# Revit family: RLV-S_Straight_DN15_External_RFA
name_source: partatom
category: Pipe Accessories
units: mm (PartAtom-declared; Revit-internal decimal feet)

## family parameters
Always vertical = Yes
Cut with Voids When Loaded = No
OmniClass Number = 23.65.55.14.17
OmniClass Title = Adjusting/Controlling Valves for Liquid Services
Part Type = Valve - Breaks Into
Round Connector Dimension = Use Diameter
Shared = No
Work Plane-Based = No

## types (2) — shared parameters
CenSd_S11_6 = 13.1 mm
CenSd_S22_6 = 15 mm  [stored 0.0492126 ft]
Connection = External thread
D = 15 mm  [stored 0.0492126 ft]
D2 = 19 mm  [stored 0.062336 ft]
D4 = 22 mm  [stored 0.0721785 ft]
D5 = 21.5 mm  [stored 0.0705381 ft]
D6 = 26.5 mm  [stored 0.0869423 ft]
DR = 20 mm  [stored 0.0656168 ft]
Description = Lockshield Valve
H2 = 21.5 mm  [stored 0.0705381 ft]
HT = 28 mm  [stored 0.0918635 ft]
IfcExportAs = IfcValveType
IfcExportType = RLV-S
Kvs = 2.2 m³/h
L2 = 22 mm  [stored 0.0721785 ft]
L3 = 7 mm  [stored 0.0229659 ft]
LOD 200 = No
LOD 350 = Yes
Manufacturer = Danfoss
Max Medium Temperature = 120 ˚C
Max Operating Pressure = 10 bar
R2 = 9.25 mm  [stored 0.0303478 ft]
RD2 = 9.5 mm  [stored 0.031168 ft]
RD5 = 10.75 mm  [stored 0.035269 ft]
RT1 = 11.2 mm  [stored 0.0367454 ft]
RV1 = 10.47 mm  [stored 0.0343504 ft]
R_thread1 = 13.22 mm  [stored 0.0433727 ft]
S11 = 15.13 mm  [stored 0.0496391 ft]
S22 = 17.32 mm
T2 = 3.5 mm  [stored 0.0114829 ft]
URL = https://store.danfoss.com
Valve Body Material = Danfoss Nickel Plated Brass
W2D = 10 mm  [stored 0.0328084 ft]
X = 11.5 mm  [stored 0.0377297 ft]
X1 = 7 mm  [stored 0.0229659 ft]
X1__ve = -7 mm  [stored -0.0229659 ft]
X2 = 39.2 mm
X5 = -10 mm  [stored -0.0328084 ft]
external(200) = No
nut(200) = No

## per-type parameters (varying)
| type | L | L4 | L5 | L6 | LL | LL1 | LL2 | Model | Model Type | RB | V1 | V2 | W | Weight | nut(350) | tailpiece |
| RLV-S_Straight_DN15_External_Tailpiece_003L0354 | 81.08 mm  [stored 0.26601 ft] | 3.5 mm  [stored 0.0114829 ft] | 10.5 mm  [stored 0.0344488 ft] | 3.64 mm  [stored 0.0119423 ft] | 32.15 mm  [stored 0.105479 ft] | 27.64 mm  [stored 0.0906824 ft] | 59.79 mm | 003L0354 | RLV-S_Straight_DN15_External_Tailpiece | 14.83 mm | 0 mm  [stored 0 ft] | 0 mm  [stored 0 ft] | 30 mm  [stored 0.0984252 ft] | 0.20 kg | Yes | Yes |
| RLV-S_Straight_DN15_External_003L0454 | 53 mm  [stored 0.173885 ft] | 2.5 mm  [stored 0.0082021 ft] | 22.4 mm  [stored 0.0734908 ft] | 7.25 mm  [stored 0.0237861 ft] | 20.85 mm  [stored 0.0684055 ft] | 32.15 mm  [stored 0.105479 ft] | 53 mm  [stored 0.173885 ft] | 003L0454 | RLV-S_Straight_DN15_External | 13.22 mm  [stored 0.0433727 ft] | 1 mm  [stored 0.00328084 ft] | 1 mm  [stored 0.00328084 ft] | 26.5 mm  [stored 0.0869423 ft] | 0.12 kg | No | No |

note: [stored X ft] marks values corroborated as IEEE doubles in the binary element streams (Revit-internal decimal feet)

## geometry (parser evidence)
native form markers: Sweep x4
no freeform markers — native parametric forms only
